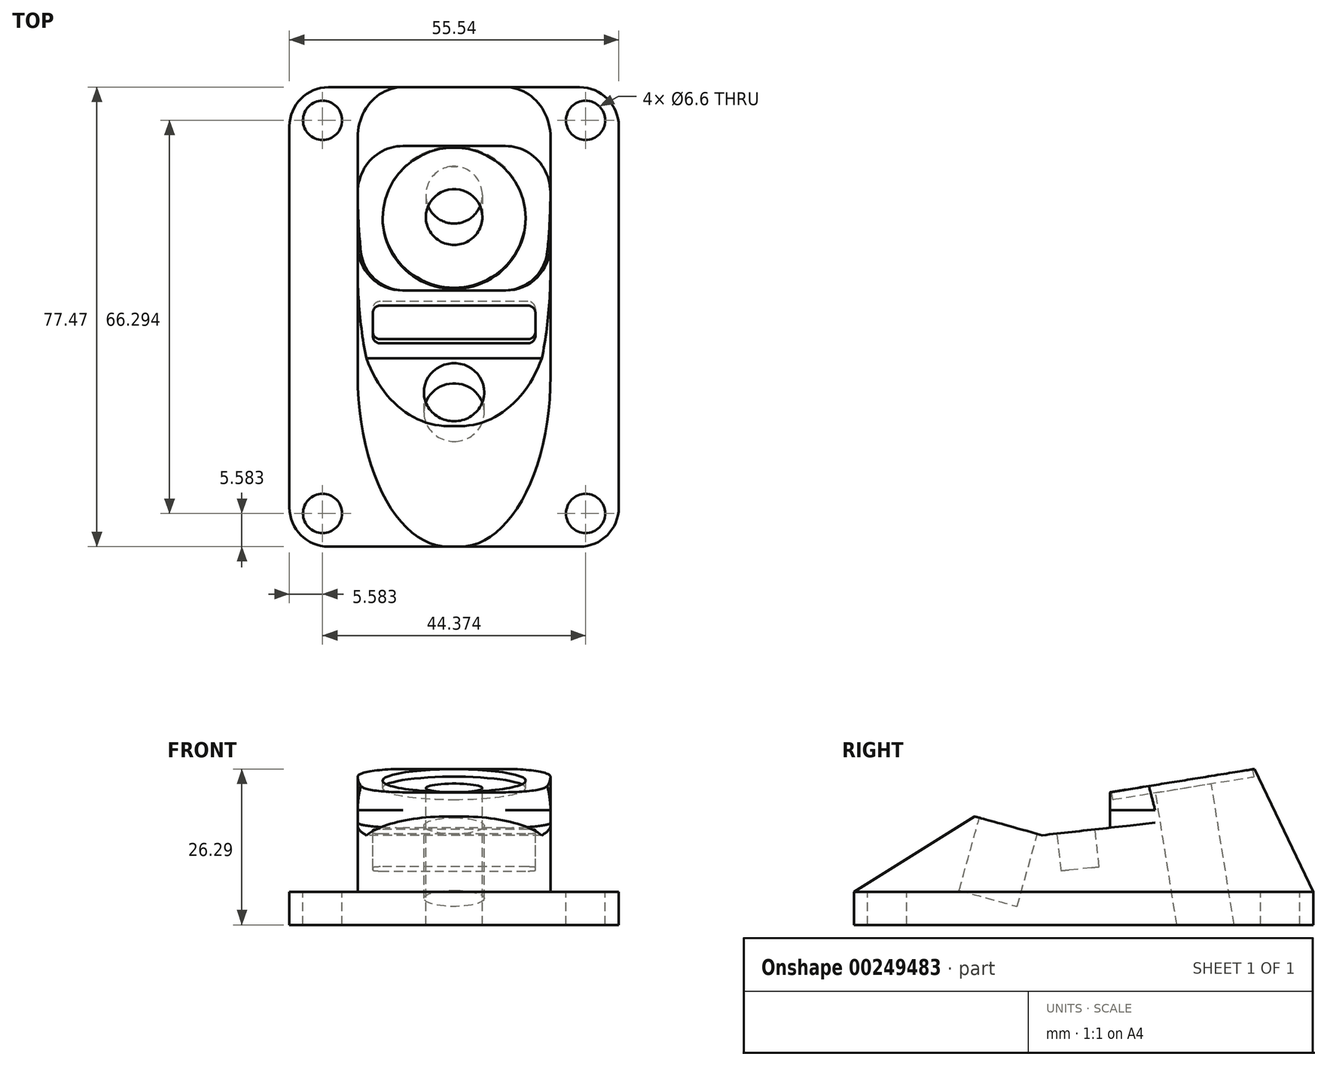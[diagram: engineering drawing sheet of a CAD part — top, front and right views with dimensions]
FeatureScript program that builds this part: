
annotation { "Feature Type Name" : "Feature", "Feature Type Description" : "" }
export const myFeature = defineFeature(function(context is Context, id is Id, definition is map)
    precondition{}
    {
        {
            var Q0;
            Q0=qCreatedBy(makeId("Top.planeOp"),FACE);
            var sketch = newSketch(context, id + "F0", { "sketchPlane" : qUnion([Q0])});
            skLineSegment(sketch, "E0.bottom", {"start": v(-21.17, 38.73) * mm, "end": v(21.17, 38.73) * mm});
            skLineSegment(sketch, "E0.top", {"start": v(-21.17, -38.73) * mm, "end": v(21.17, -38.73) * mm});
            skLineSegment(sketch, "E0.left", {"start": v(-27.77, 32.13) * mm, "end": v(-27.77, -32.13) * mm});
            skLineSegment(sketch, "E0.right", {"start": v(27.77, 32.13) * mm, "end": v(27.77, -32.13) * mm});
            skPoint(sketch, "E1.visualSharp", {"position": v(-27.77, 38.73) * mm});
            skArc(sketch, "E1.filletArc", {"start": v(-21.17, 38.73) * mm, "mid": v(-25.84, 36.8) * mm, "end": v(-27.77, 32.13) * mm});
            skPoint(sketch, "E2.visualSharp", {"position": v(27.77, 38.73) * mm});
            skArc(sketch, "E2.filletArc", {"start": v(27.77, 32.13) * mm, "mid": v(25.84, 36.8) * mm, "end": v(21.17, 38.74) * mm});
            skPoint(sketch, "E3.visualSharp", {"position": v(27.77, -38.73) * mm});
            skArc(sketch, "E3.filletArc", {"start": v(21.17, -38.73) * mm, "mid": v(25.84, -36.8) * mm, "end": v(27.77, -32.13) * mm});
            skPoint(sketch, "E4.visualSharp", {"position": v(-27.77, -38.73) * mm});
            skArc(sketch, "E4.filletArc", {"start": v(-27.77, -32.13) * mm, "mid": v(-25.84, -36.8) * mm, "end": v(-21.17, -38.74) * mm});
            skSolve(sketch);
        }
        {
            var Q0;
            Q0 = qSketchRegion(id + "F0", true);
            extrude(context, id + "F1", {"entities" : qUnion([Q0]), "depth" : 5.6 * mm});
        }
        {
            var Q0;
            Q0=makeQuery(id+"F1.opExtrude","CAP_FACE",FACE,{"disambiguationData":[OSD([sQuery(id+"F0.wireOp",EDGE,"E0.bottom"),sQuery(id+"F0.wireOp",EDGE,"E0.top"),sQuery(id+"F0.wireOp",EDGE,"E0.left"),sQuery(id+"F0.wireOp",EDGE,"E0.right"),sQuery(id+"F0.wireOp",EDGE,"E1.filletArc"),sQuery(id+"F0.wireOp",EDGE,"E2.filletArc"),sQuery(id+"F0.wireOp",EDGE,"E3.filletArc"),sQuery(id+"F0.wireOp",EDGE,"E4.filletArc")])],"isStart":false});
            var sketch = newSketch(context, id + "F2", { "sketchPlane" : qUnion([Q0])});
            skPoint(sketch, "E5", {"position": v(-22.19, 33.15) * mm});
            skPoint(sketch, "E6", {"position": v(22.19, 33.15) * mm});
            skPoint(sketch, "E7", {"position": v(22.19, -33.15) * mm});
            skPoint(sketch, "E8", {"position": v(-22.19, -33.15) * mm});
            skSolve(sketch);
        }
        {
            var Q0;
            Q0=sQuery(id+"F2.wireOp",VERTEX,"E5");
            var Q1;
            Q1=sQuery(id+"F2.wireOp",VERTEX,"E6");
            var Q2;
            Q2=sQuery(id+"F2.wireOp",VERTEX,"E7");
            var Q3;
            Q3=sQuery(id+"F2.wireOp",VERTEX,"E8");
            var Q4;
            Q4=makeQuery(id+"F1.opExtrude","SWEPT_BODY",BODY,{"disambiguationData":[OSD([sQuery(id+"F0.wireOp",EDGE,"E0.bottom"),sQuery(id+"F0.wireOp",EDGE,"E0.top"),sQuery(id+"F0.wireOp",EDGE,"E0.left"),sQuery(id+"F0.wireOp",EDGE,"E0.right"),sQuery(id+"F0.wireOp",EDGE,"E1.filletArc"),sQuery(id+"F0.wireOp",EDGE,"E2.filletArc"),sQuery(id+"F0.wireOp",EDGE,"E3.filletArc"),sQuery(id+"F0.wireOp",EDGE,"E4.filletArc")])]});
            hole(context, id + "F3", {"style" : HoleStyle.SIMPLE, "endStyle" : HoleEndStyle.THROUGH, "holeDiameter" : 6.6 * mm, "tappedDepth" : 12.7 * mm, "tapClearance" : 3, "locations" : qUnion([Q0, Q1, Q2, Q3]), "scope" : qUnion([Q4])});
        }
        {
            var Q0;
            Q0=qCreatedBy(makeId("Right.planeOp"),FACE);
            var sketch = newSketch(context, id + "F4", { "sketchPlane" : qUnion([Q0])});
            skLineSegment(sketch, "E9", {"start": v(-38.73, 5.59) * mm, "end": v(-18.41, 18.29) * mm});
            skLineSegment(sketch, "E10", {"start": v(-18.41, 18.29) * mm, "end": v(-6.98, 15.11) * mm});
            skLineSegment(sketch, "E11", {"start": v(-6.98, 15.11) * mm, "end": v(4.45, 16.38) * mm});
            skLineSegment(sketch, "E12", {"start": v(4.45, 22.35) * mm, "end": v(28.83, 26.29) * mm});
            skLineSegment(sketch, "E13", {"start": v(28.83, 26.29) * mm, "end": v(38.73, 5.59) * mm});
            skLineSegment(sketch, "E14", {"start": v(4.45, 22.35) * mm, "end": v(4.45, 16.38) * mm});
            skLineSegment(sketch, "E15", {"start": v(-38.73, 5.59) * mm, "end": v(38.73, 5.59) * mm});
            skSolve(sketch);
        }
        {
            var Q0;
            Q0 = qSketchRegion(id + "F4", true);
            extrude(context, id + "F5", {"entities" : qUnion([Q0]), "operationType" : NewBodyOperationType.ADD, "endBound" : BoundingType.SYMMETRIC, "depth" : 32.5 * mm});
        }
        {
            var Q0;
            Q0=makeQuery(id+"F5.opExtrude","SWEPT_FACE",FACE,{"disambiguationData":[OSD([sQuery(id+"F4.wireOp",EDGE,"E11")])]});
            var sketch = newSketch(context, id + "F6", { "sketchPlane" : qUnion([Q0])});
            skLineSegment(sketch, "E16.0", {"start": v(-13.72, 3.69) * mm, "end": v(-13.72, -2.73) * mm});
            skLineSegment(sketch, "E16.1", {"start": v(13.72, 3.69) * mm, "end": v(-13.72, 3.69) * mm});
            skLineSegment(sketch, "E16.2", {"start": v(13.72, -2.73) * mm, "end": v(13.72, 3.69) * mm});
            skLineSegment(sketch, "E16.3", {"start": v(-13.72, -2.73) * mm, "end": v(13.72, -2.73) * mm});
            skSolve(sketch);
        }
        {
            var Q0;
            Q0 = qSketchRegion(id + "F6", true);
            extrude(context, id + "F7", {"entities" : qUnion([Q0]), "operationType" : NewBodyOperationType.REMOVE, "oppositeDirection" : true, "depth" : 6.35 * mm});
        }
        {
            var Q0;
            Q0=makeQuery(id+"F5.opExtrude","CAP_EDGE",EDGE,{"disambiguationData":[OSD([sQuery(id+"F4.wireOp",EDGE,"E9")])],"isStart":true});
            var Q1;
            Q1=makeQuery(id+"F5.opExtrude","CAP_EDGE",EDGE,{"disambiguationData":[OSD([sQuery(id+"F4.wireOp",EDGE,"E9")])],"isStart":false});
            fillet(context, id + "F8", {"entities" : qUnion([Q0, Q1]), "radius" : 15.24 * mm, "tangentPropagation" : true, "allowEdgeOverflow" : false});
        }
        {
            var Q0;
            Q0=makeQuery(id+"F7.boolean.opBoolean","COPY",EDGE,{"derivedFrom":makeQuery(id+"F7.opExtrude","SWEPT_EDGE",EDGE,{"disambiguationData":[OSD([sQuery(id+"F6.wireOp",EDGE,"E16.1"),sQuery(id+"F6.wireOp",EDGE,"E16.2")])]})});
            var Q1;
            Q1=makeQuery(id+"F7.boolean.opBoolean","COPY",EDGE,{"derivedFrom":makeQuery(id+"F7.opExtrude","SWEPT_EDGE",EDGE,{"disambiguationData":[OSD([sQuery(id+"F6.wireOp",EDGE,"E16.2"),sQuery(id+"F6.wireOp",EDGE,"E16.3")])]})});
            var Q2;
            Q2=makeQuery(id+"F7.boolean.opBoolean","COPY",EDGE,{"derivedFrom":makeQuery(id+"F7.opExtrude","SWEPT_EDGE",EDGE,{"disambiguationData":[OSD([sQuery(id+"F6.wireOp",EDGE,"E16.0"),sQuery(id+"F6.wireOp",EDGE,"E16.1")])]})});
            var Q3;
            Q3=makeQuery(id+"F7.boolean.opBoolean","COPY",EDGE,{"derivedFrom":makeQuery(id+"F7.opExtrude","SWEPT_EDGE",EDGE,{"disambiguationData":[OSD([sQuery(id+"F6.wireOp",EDGE,"E16.0"),sQuery(id+"F6.wireOp",EDGE,"E16.3")])]})});
            fillet(context, id + "F9", {"entities" : qUnion([Q0, Q1, Q2, Q3]), "radius" : 1.27 * mm, "tangentPropagation" : true, "allowEdgeOverflow" : false});
        }
        {
            var Q0;
            Q0=makeQuery(id+"F5.opExtrude","CAP_EDGE",EDGE,{"disambiguationData":[OSD([sQuery(id+"F4.wireOp",EDGE,"E13")])],"isStart":false});
            var Q1;
            Q1=makeQuery(id+"F8.opFillet","BLEND_EDGE",EDGE,{"blendedFrom":[makeQuery(id+"F5.opExtrude","CAP_EDGE",EDGE,{"disambiguationData":[OSD([sQuery(id+"F4.wireOp",EDGE,"E9")])],"isStart":false}),makeQuery(id+"F5.opExtrude","SWEPT_FACE",FACE,{"disambiguationData":[OSD([sQuery(id+"F4.wireOp",EDGE,"E14")])]})],"blendedInto":[makeQuery(id+"F5.opExtrude","SWEPT_FACE",FACE,{"disambiguationData":[OSD([sQuery(id+"F4.wireOp",EDGE,"E14")])]})]});
            var Q2;
            Q2=makeQuery(id+"F8.opFillet","BLEND_EDGE",EDGE,{"blendedFrom":[makeQuery(id+"F5.opExtrude","CAP_EDGE",EDGE,{"disambiguationData":[OSD([sQuery(id+"F4.wireOp",EDGE,"E9")])],"isStart":true}),makeQuery(id+"F5.opExtrude","SWEPT_FACE",FACE,{"disambiguationData":[OSD([sQuery(id+"F4.wireOp",EDGE,"E14")])]})],"blendedInto":[makeQuery(id+"F5.opExtrude","SWEPT_FACE",FACE,{"disambiguationData":[OSD([sQuery(id+"F4.wireOp",EDGE,"E14")])]})]});
            var Q3;
            Q3=makeQuery(id+"F5.opExtrude","CAP_EDGE",EDGE,{"disambiguationData":[OSD([sQuery(id+"F4.wireOp",EDGE,"E13")])],"isStart":true});
            fillet(context, id + "F10", {"entities" : qUnion([Q0, Q1, Q2, Q3]), "radius" : 7.62 * mm, "tangentPropagation" : true, "allowEdgeOverflow" : false});
        }
        {
            var Q0;
            Q0=makeQuery(id+"F5.opExtrude","SWEPT_FACE",FACE,{"disambiguationData":[OSD([sQuery(id+"F4.wireOp",EDGE,"E12")])]});
            var sketch = newSketch(context, id + "F11", { "sketchPlane" : qUnion([Q0])});
            skCircle(sketch, "E17", {"center": v(0, 20.3) * mm, "radius": 4.76 * mm});
            skSolve(sketch);
        }
        {
            var Q0;
            Q0 = qSketchRegion(id + "F11", true);
            extrude(context, id + "F12", {"entities" : qUnion([Q0]), "operationType" : NewBodyOperationType.REMOVE, "oppositeDirection" : true, "depth" : 25.4 * mm});
        }
        {
            var Q0;
            Q0=makeQuery(id+"F5.opExtrude","SWEPT_FACE",FACE,{"disambiguationData":[OSD([sQuery(id+"F4.wireOp",EDGE,"E10")])]});
            var sketch = newSketch(context, id + "F13", { "sketchPlane" : qUnion([Q0])});
            skCircle(sketch, "E18", {"center": v(0, -16.7) * mm, "radius": 5.08 * mm});
            skSolve(sketch);
        }
        {
            var Q0;
            Q0 = qSketchRegion(id + "F13", true);
            extrude(context, id + "F14", {"entities" : qUnion([Q0]), "operationType" : NewBodyOperationType.REMOVE, "oppositeDirection" : true, "depth" : 12.7 * mm});
        }
        {
            var Q0;
            Q0=makeQuery(id+"F5.opExtrude","SWEPT_FACE",FACE,{"disambiguationData":[OSD([sQuery(id+"F4.wireOp",EDGE,"E12")])]});
            var sketch = newSketch(context, id + "F15", { "sketchPlane" : qUnion([Q0])});
            skCircle(sketch, "E19", {"center": v(0, 20.3) * mm, "radius": 12.06 * mm});
            skSolve(sketch);
        }
        {
            var Q0;
            Q0 = qSketchRegion(id + "F15", true);
            extrude(context, id + "F16", {"entities" : qUnion([Q0]), "operationType" : NewBodyOperationType.REMOVE, "oppositeDirection" : true, "depth" : 1.27 * mm});
        }
    });
